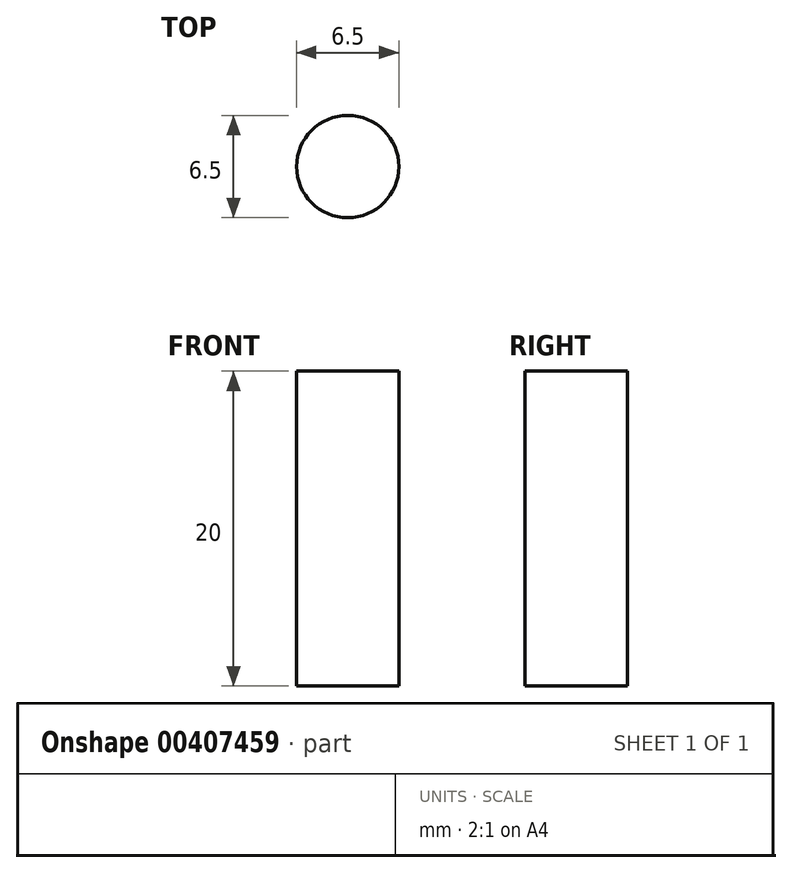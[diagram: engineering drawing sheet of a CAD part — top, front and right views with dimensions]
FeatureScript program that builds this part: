
annotation { "Feature Type Name" : "Feature", "Feature Type Description" : "" }
export const myFeature = defineFeature(function(context is Context, id is Id, definition is map)
    precondition{}
    {
        {
            var Q0;
            Q0=qCreatedBy(makeId("Top.planeOp"),FACE);
            var sketch = newSketch(context, id + "F0", { "sketchPlane" : qUnion([Q0])});
            skCircle(sketch, "E0", {"center": v(0, 0) * mm, "radius": 3.25 * mm});
            skSolve(sketch);
        }
        {
            var Q0;
            Q0=makeQuery(id+"F0.imprint","IMPRINT",FACE,{"disambiguationData":[TD([[makeQuery(id+"F0.imprint","IMPRINT",EDGE,{"derivedFrom":sQuery(id+"F0.wireOp",EDGE,"E0")}),1.0]])]});
            extrude(context, id + "F1", {"entities" : qUnion([Q0]), "depth" : 20 * mm});
        }
    });
